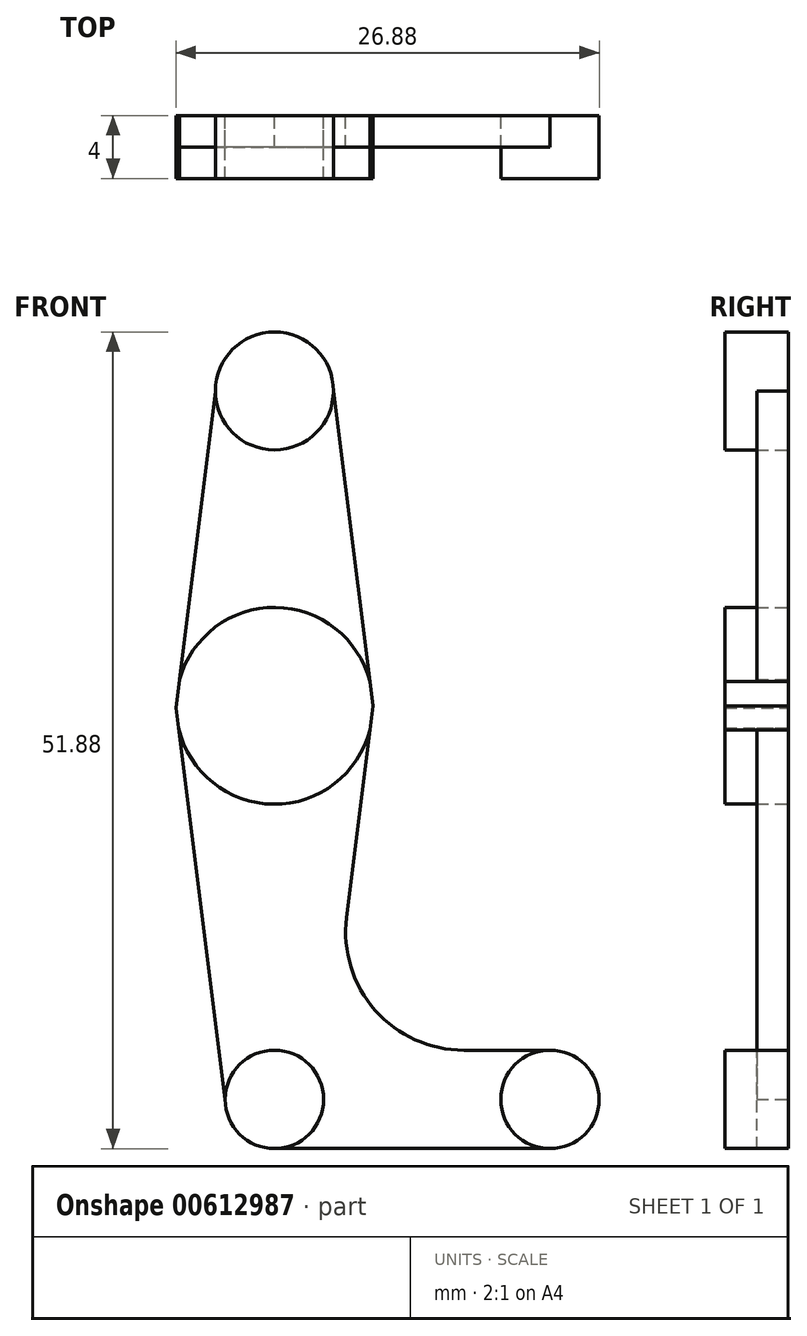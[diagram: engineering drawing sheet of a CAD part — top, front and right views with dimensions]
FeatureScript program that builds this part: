
annotation { "Feature Type Name" : "Feature", "Feature Type Description" : "" }
export const myFeature = defineFeature(function(context is Context, id is Id, definition is map)
    precondition{}
    {
        {
            var Q0;
            Q0=qCreatedBy(makeId("Front.planeOp"),FACE);
            var sketch = newSketch(context, id + "F0", { "sketchPlane" : qUnion([Q0])});
            skCircle(sketch, "E0", {"center": v(0, 0) * mm, "radius": 3.75 * mm});
            skCircle(sketch, "E1", {"center": v(0, -20) * mm, "radius": 6.25 * mm});
            skCircle(sketch, "E2", {"center": v(0, -45) * mm, "radius": 3.12 * mm});
            skCircle(sketch, "E3", {"center": v(17.5, -45) * mm, "radius": 3.12 * mm});
            skLineSegment(sketch, "E4", {"start": v(0, 0) * mm, "end": v(0, -45) * mm, "construction": true});
            skLineSegment(sketch, "E5", {"start": v(17.5, -45) * mm, "end": v(0, -45) * mm, "construction": true});
            skLineSegment(sketch, "E6", {"start": v(-3.75, 0) * mm, "end": v(-6.25, -20.13) * mm});
            skLineSegment(sketch, "E7", {"start": v(-6.25, -20.13) * mm, "end": v(-3.12, -45) * mm});
            skLineSegment(sketch, "E8", {"start": v(3.75, 0) * mm, "end": v(6.25, -20) * mm});
            skLineSegment(sketch, "E9", {"start": v(6.25, -20) * mm, "end": v(4.58, -33.45) * mm});
            skLineSegment(sketch, "E10", {"start": v(0, -48.12) * mm, "end": v(17.5, -48.12) * mm});
            skLineSegment(sketch, "E11", {"start": v(12.02, -41.87) * mm, "end": v(17.5, -41.87) * mm});
            skArc(sketch, "E12", {"start": v(4.58, -33.45) * mm, "mid": v(6.4, -39.34) * mm, "end": v(12.02, -41.87) * mm});
            skSolve(sketch);
        }
        {
            var Q0;
            {var subQ0=sQuery(id+"F0.wireOp",EDGE,"E6");var subQ1=sQuery(id+"F0.wireOp",EDGE,"E0");var subQ2=makeQuery(id+"F0.imprint","INTERSECT",VERTEX,{"derivedFrom":[subQ1,subQ0]});Q0=makeQuery(id+"F0.imprint","IMPRINT",FACE,{"disambiguationData":[TD([[makeQuery(id+"F0.imprint","IMPRINT",EDGE,{"disambiguationData":[TD([[subQ2,-1.0]])],"derivedFrom":subQ1}),-1.0]])]});}
            var Q1;
            {var subQ5=sQuery(id+"F0.wireOp",EDGE,"E10");Q1=makeQuery(id+"F0.imprint","IMPRINT",FACE,{"disambiguationData":[TD([[makeQuery(id+"F0.imprint","IMPRINT",EDGE,{"derivedFrom":subQ5}),1.0]])]});}
            extrude(context, id + "F1", {"entities" : qUnion([Q0, Q1]), "depth" : 2 * mm, "offsetDistance" : 25 * mm});
        }
        {
            var Q0;
            {var subQ0=sQuery(id+"F0.wireOp",EDGE,"E0");var subQ1=makeQuery(id+"F0.imprint","INTERSECT",VERTEX,{"derivedFrom":[subQ0,sQuery(id+"F0.wireOp",EDGE,"E6")]});Q0=makeQuery(id+"F0.imprint","IMPRINT",FACE,{"disambiguationData":[TD([[makeQuery(id+"F0.imprint","IMPRINT",EDGE,{"disambiguationData":[TD([[subQ1,1.0]])],"derivedFrom":subQ0}),1.0]])]});}
            var Q1;
            {var subQ2=sQuery(id+"F0.wireOp",EDGE,"E1");var subQ5=sQuery(id+"F0.wireOp",EDGE,"E8");var subQ6=makeQuery(id+"F0.imprint","INTERSECT",VERTEX,{"derivedFrom":[subQ2,subQ5]});Q1=makeQuery(id+"F0.imprint","IMPRINT",FACE,{"disambiguationData":[TD([[makeQuery(id+"F0.imprint","IMPRINT",EDGE,{"disambiguationData":[TD([[subQ6,-1.0]])],"derivedFrom":subQ2}),1.0]])]});}
            var Q2;
            {var subQ0=sQuery(id+"F0.wireOp",EDGE,"E2");var subQ1=makeQuery(id+"F0.imprint","INTERSECT",VERTEX,{"derivedFrom":[subQ0,sQuery(id+"F0.wireOp",EDGE,"E7")]});Q2=makeQuery(id+"F0.imprint","IMPRINT",FACE,{"disambiguationData":[TD([[makeQuery(id+"F0.imprint","IMPRINT",EDGE,{"disambiguationData":[TD([[subQ1,-1.0]])],"derivedFrom":subQ0}),1.0]])]});}
            var Q3;
            {var subQ0=sQuery(id+"F0.wireOp",EDGE,"E3");var subQ1=makeQuery(id+"F0.imprint","INTERSECT",VERTEX,{"derivedFrom":[subQ0,sQuery(id+"F0.wireOp",EDGE,"E10")]});Q3=makeQuery(id+"F0.imprint","IMPRINT",FACE,{"disambiguationData":[TD([[makeQuery(id+"F0.imprint","IMPRINT",EDGE,{"disambiguationData":[TD([[subQ1,1.0]])],"derivedFrom":subQ0}),1.0]])]});}
            extrude(context, id + "F2", {"entities" : qUnion([Q0, Q1, Q2, Q3]), "depth" : 4 * mm, "offsetDistance" : 25 * mm});
        }
    });
